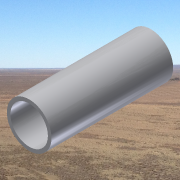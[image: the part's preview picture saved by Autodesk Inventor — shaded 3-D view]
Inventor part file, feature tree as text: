
AUTODESK INVENTOR PART (.ipt)
format: ipt  version: 2014 SP1 (Build 180222100, 222)  size: 170,496 bytes
history: native  units: in
note: dims shown in document units (in); Inventor stores cm internally (conversion verified against a paired STEP export)
features: extrude x4, sketch x4
ambient origin geometry x8: Origin, YZ Plane, XZ Plane, XY Plane, X Axis, Y Axis, Z Axis, Center Point
bodies: Solid1 (feature_tree)
feature tree (8):
  extrude  "mainBody"  Depth=3.4062in TaperAngle=0.0deg
  extrude  "mainTube"  Depth=7.0in TaperAngle=0.0deg
  extrude  "mainSocket1"  Depth=1.0in TaperAngle=0.0deg
  extrude  "mainSocket2"  Depth=1.0in TaperAngle=0.0deg
  sketch  "Sketch1"  dims[d0=1.25in d1=3.4062in d2=0.0in]
  sketch  "Sketch14"  dims[d43=0.824in d45=7.0in d46=0.0in]
  sketch  "Sketch15"  dims[d47=1.05in d49=1.0in d50=0.0in]
  sketch  "Sketch16"  dims[d51=1.05in d53=1.0in d54=0.0in]
